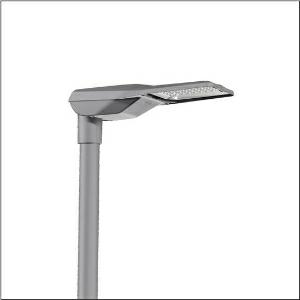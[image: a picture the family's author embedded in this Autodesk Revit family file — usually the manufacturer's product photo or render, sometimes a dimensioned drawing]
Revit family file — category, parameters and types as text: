
# Revit family: streetlight_sl_21_iq_mini___st0_8a_5xe2c31g08gb_0650
name_source: partatom
category: Lighting Fixtures
units: mm (PartAtom-declared; Revit-internal decimal feet)

## family parameters
Cut with Voids When Loaded = No
Host = Face
Light Source = No
Part Type = Normal
Room Calculation Point = No
Round Connector Dimension = Use Diameter
Shared = No

## types (1)
- --- (1 x LED, 5680 lm, 37.1 W, 3000K)
    Apparent Load = 37 VA
    CIE Flux Codes = 38 75 97 100 100
    Color Rendering = 70
    Color Temperature = 3000K
    Default Elevation = 1800 mm
    Description = Streetlight SL 21 iQ mini, mast luminaire, primary light control with lens, of PMMA, primary optical cover: cover, of toughened safety glass, transparent, light distribution: ST0.8a, light emission: direct distribution, primary light characteristic: asymmetric, installation type: post-top, side-entry, LED, High Power LED, rated luminous flux: 5.680lm, luminous efficacy: 153lm/W, light colour: 730, colour temperature: 3000K, control gear: iQ Street-Remote, control: Street-Remote, Auto-Match, Temp-Guard, Lumen-Switch, Night-Set, Smart-Wire, Light-Fading, Desk-Remote (wireless, voltage-free reading and setting of iQ features in the workshop via application-optimized NFC function/RFID function), optimised constant luminous flux control (CLO 2.0), pre-setting: linear dimming characteristic, mains connection: 220..240V, AC, 50/60Hz, start of lifetime: 37W, end of service life: 39W, reduction: 18W, luminaire housing, of diecast aluminium, powder-coated, Siteco® metallic grey (DB 702S), corrosivity category C5 mid according to DIN EN ISO 12944, please order mast flange separately, inclination adjustable: 0°, 5°, 10°, 15°, sealing non-destructively replaceable, multi-level sealing system, length: 628mm, width: 235mm, height: 110mm, mast flange for spigot size: 42mm (side-entry): 5XC10008XM4, 60/48mm (side-entry/post-top): 5XC10108XM2, 76/60mm (side-entry/post-top): 5XC10108XM1, mounting height: 4..8m, protection rating (complete): IP66, insulation class (complete): insulation class II (safety insulation), certification: CE, ENEC, ENEC+, VDE, impact resistance: IK10, permissible operating ambient temperature for outdoor applications: -40..+50°C, standard-compliant lighting for roads and squares, packaging unit: 1 piece

Light Distribution: ST0.8a
    Height = 110 mm
    Lamp = 1 x LED
    Lamp Light Flux = 5680 lm
    Lamp Power = 37.1 W
    Lamp count = 1
    Length = 625 mm
    Luminous efficacy = 153 lm/W
    Manufacturer = Siteco
    ModVariant = No
    Model = 5XE2C31G08GB
    Number of Poles = 1
    OnlyDefault = Yes
    Power Factor = 1
    Product Name = Streetlight SL 21 iQ mini | ST0.8a
    Product group = mast luminaire | pylon top
    ProductGroupID = 6100
    Protection Class = Protection class II
    Protection Degree = IP 66
    RLX_Detail_Level = 1
    RLX_Emergency_Light_Flux = 0 lm
    RLX_Emergency_Type = 0
    RLX_Emergency_Type_DB = No
    RlxData = <blob elided: 26365 chars, md5=5afc4370>
    Socket = socket
    Standby Power = 0 W
    System Light Flux = 5680 lm
    System Power = 37 W
    Type Comments = factory setting: luminous flux: 100 % | dim-lin: 254 | 385 mA
    Type Image = l_1003519.jpg
    URL = http://relux.com
    VarID = @adj_185678
    Voltage = 0 V
    Weight = 0.00 kg
    Width = 234 mm

## geometry (parser evidence)
native form markers: Blend x4, Sweep x10
no freeform markers — native parametric forms only
